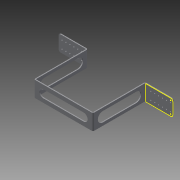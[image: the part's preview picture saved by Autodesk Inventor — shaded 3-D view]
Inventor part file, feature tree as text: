
AUTODESK INVENTOR PART (.ipt)
format: ipt  version: 2014 SP1 (Build 180222100, 222)  size: 382,976 bytes
history: native  units: in
note: dims shown in document units (in); Inventor stores cm internally (conversion verified against a paired STEP export)
features: sheet_metal_op x7, sketch x7, other x6, reference x3, extrude x2, chamfer x1
ambient origin geometry x8: Origin, YZ Plane, XZ Plane, XY Plane, X Axis, Y Axis, Z Axis, Center Point
bodies: Solid1 (feature_tree)
feature tree (26):
  sheet_metal_op  "Face1"
  sheet_metal_op  "Flange1"
  sheet_metal_op  "Flange2"
  chamfer  "Corner Round1"
  sketch  "Sketch4"  dims[d5=0.25in]
  extrude  "Extrusion1"  Depth=2.0in
  sketch  "Sketch1"  dims[d0=7.25in d1=2.0in]
  other  "Plate1"
  sketch  "Sketch2"  dims[d2=0.125in d3=0.125in]
  other  "Plate2"
  sheet_metal_op  "Bend1"
  sheet_metal_op  "Corner1"
  sketch  "Sketch3"  dims[d4=0.0625in]
  other  "Plate3"
  sheet_metal_op  "Bend2"
  sheet_metal_op  "Corner2"
  sketch  "Sketch5"  dims[d6=0.125in]
  reference  "Reference1"
  reference  "Reference2"
  reference  "Reference3"
  sketch  "Sketch6"  dims[d7=6.5in d8=90.0deg d9=0.05in]
  sketch  "Sketch7"  dims[d10=0.5in d11=0.125in d12=0.125in d13=0.125in d14=0.0625in d15=0.25in d16=0.125in d17=3.5in d18=90.0deg d19=0.05in d20=0.5in d21=0.125in d22=0.125in d23=0.25in d24=0.125in d25=0.0in d26=1.25in d27=1.0in d28=1.0665in d29=100.0in d30=0.0in d31=5.15in d32=1.0in d33=1.0in d34=1.0in d35=0.125in d36=0.0in]
  other  "Cut1"
  other  "Cut2"
  other  "Definition1"
  extrude  "Extrusion2"  Depth=0.125in
